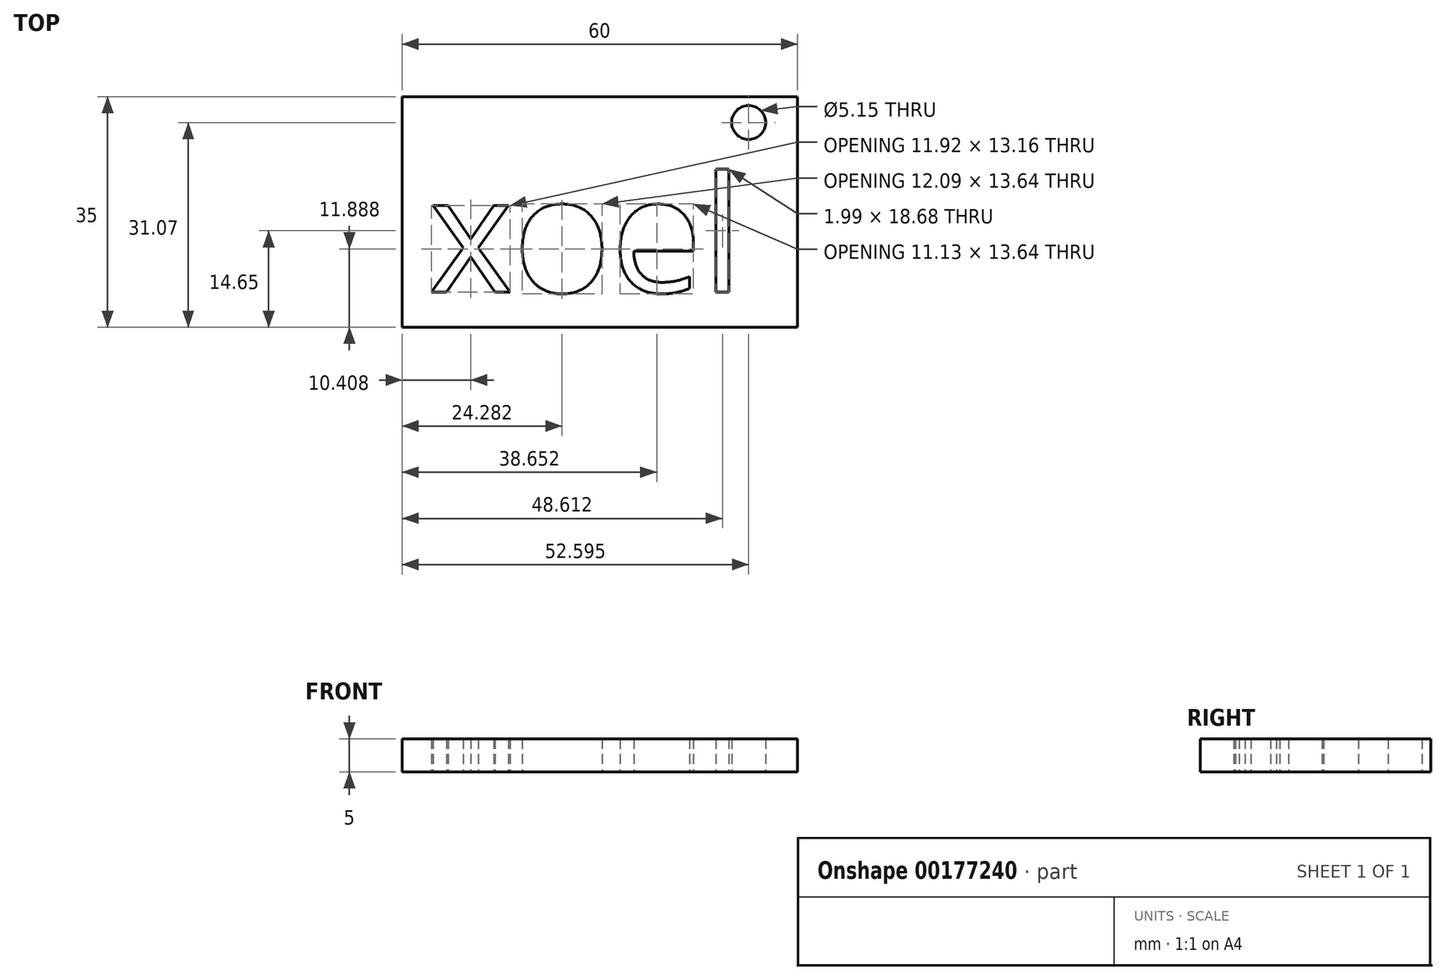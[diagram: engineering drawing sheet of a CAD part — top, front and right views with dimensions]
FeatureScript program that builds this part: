
annotation { "Feature Type Name" : "Feature", "Feature Type Description" : "" }
export const myFeature = defineFeature(function(context is Context, id is Id, definition is map)
    precondition{}
    {
        {
            var Q0;
            Q0=qCreatedBy(makeId("Top.planeOp"),FACE);
            var sketch = newSketch(context, id + "F0", { "sketchPlane" : qUnion([Q0])});
            skLineSegment(sketch, "E0.bottom", {"start": v(-60, 35) * mm, "end": v(0, 35) * mm});
            skLineSegment(sketch, "E0.top", {"start": v(-60, 0) * mm, "end": v(0, 0) * mm});
            skLineSegment(sketch, "E0.left", {"start": v(-60, 35) * mm, "end": v(-60, 0) * mm});
            skLineSegment(sketch, "E0.right", {"start": v(0, 35) * mm, "end": v(0, 0) * mm});
            skText(sketch, "E1", { "text": "xoel", "fontName": "OpenSans-Regular.ttf"});
            skCircle(sketch, "E2", {"center": v(-7.4, 31.07) * mm, "radius": 2.58 * mm});
            const initialGuessF0  = {"E1": [-0.05602, 0.00531, 1, 0, 0.0177]};
            skSetInitialGuess(sketch, initialGuessF0);
            skSolve(sketch);
        }
        {
            var Q0;
            Q0 = qSketchRegion(id + "F0", true);
            extrude(context, id + "F1", {"entities" : qUnion([Q0]), "depth" : 5 * mm});
        }
    });
